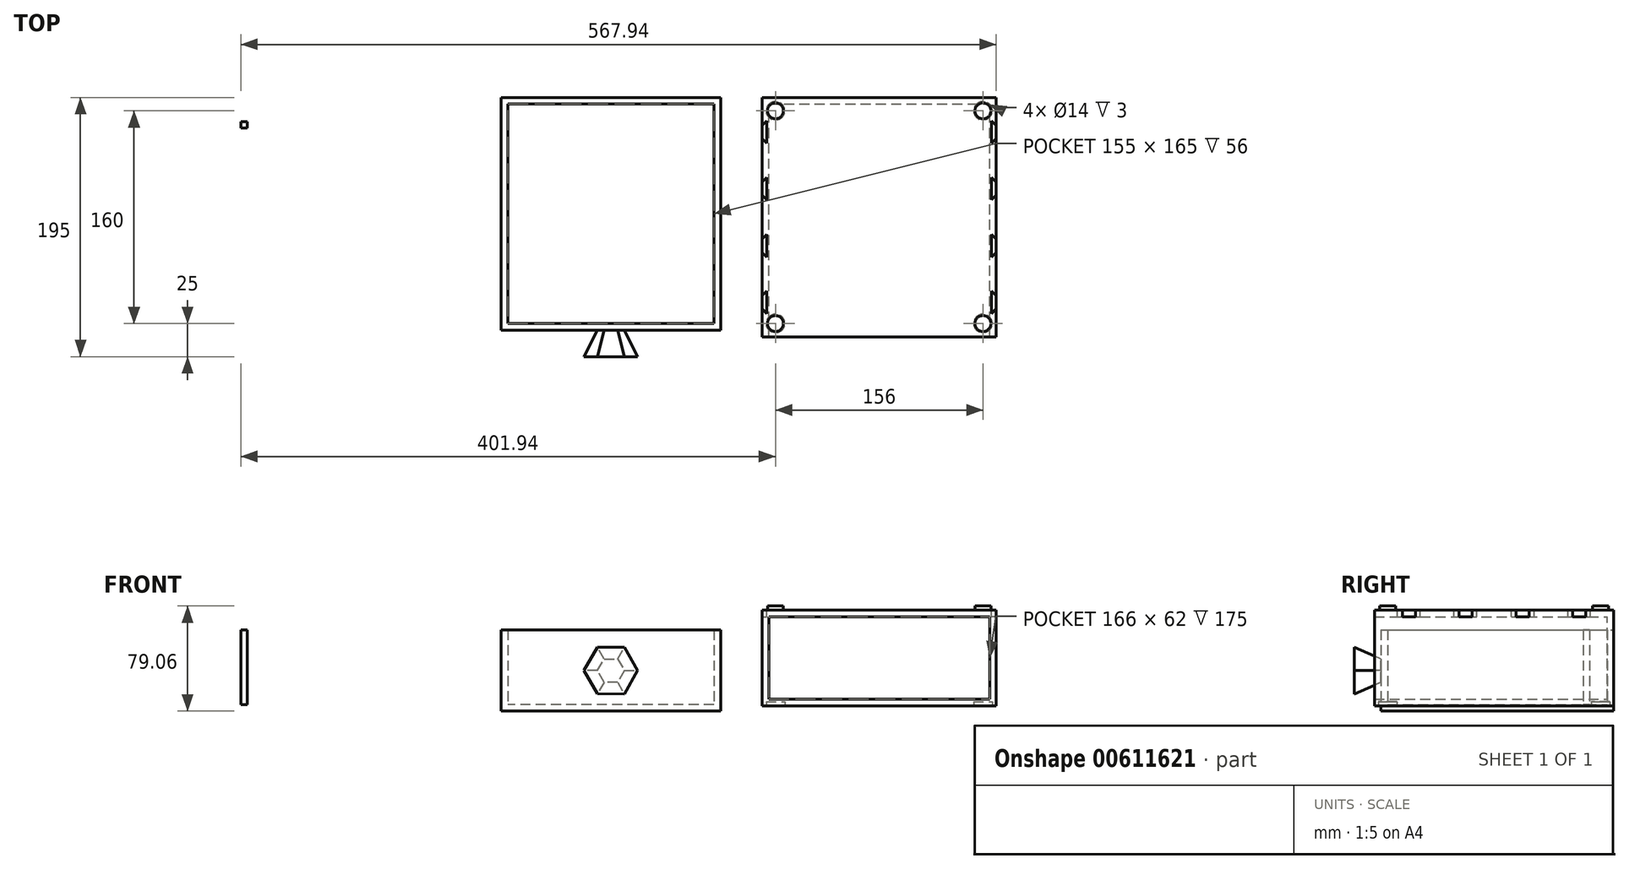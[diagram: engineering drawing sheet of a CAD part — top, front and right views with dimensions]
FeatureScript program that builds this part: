
annotation { "Feature Type Name" : "Feature", "Feature Type Description" : "" }
export const myFeature = defineFeature(function(context is Context, id is Id, definition is map)
    precondition{}
    {
        {
            var Q0;
            Q0=qCreatedBy(makeId("Front.planeOp"),FACE);
            var sketch = newSketch(context, id + "F0", { "sketchPlane" : qUnion([Q0])});
            skLineSegment(sketch, "E0.bottom", {"start": v(-21.74, -12.57) * mm, "end": v(144.26, -12.57) * mm});
            skLineSegment(sketch, "E0.top", {"start": v(-21.74, 49.43) * mm, "end": v(144.26, 49.43) * mm});
            skLineSegment(sketch, "E0.left", {"start": v(-21.74, -12.57) * mm, "end": v(-21.74, 49.43) * mm});
            skLineSegment(sketch, "E0.right", {"start": v(144.26, -12.57) * mm, "end": v(144.26, 49.43) * mm});
            skLineSegment(sketch, "E1.bottom", {"start": v(-26.74, -17.57) * mm, "end": v(149.26, -17.57) * mm});
            skLineSegment(sketch, "E1.top", {"start": v(-26.74, 54.43) * mm, "end": v(149.26, 54.43) * mm});
            skLineSegment(sketch, "E1.left", {"start": v(-26.74, -17.57) * mm, "end": v(-26.74, 54.43) * mm});
            skLineSegment(sketch, "E1.right", {"start": v(149.26, -17.57) * mm, "end": v(149.26, 54.43) * mm});
            skSolve(sketch);
        }
        {
            var Q0;
            Q0=makeQuery(id+"F0.imprint","IMPRINT",FACE,{"disambiguationData":[TD([[makeQuery(id+"F0.imprint","IMPRINT",EDGE,{"derivedFrom":sQuery(id+"F0.wireOp",EDGE,"E0.bottom")}),1.0]])]});
            extrude(context, id + "F1", {"entities" : qUnion([Q0]), "depth" : 5 * mm, "offsetDistance" : 25 * mm});
        }
        {
            var Q0;
            Q0=makeQuery(id+"F0.imprint","IMPRINT",FACE,{"disambiguationData":[TD([[makeQuery(id+"F0.imprint","IMPRINT",EDGE,{"derivedFrom":sQuery(id+"F0.wireOp",EDGE,"E0.bottom")}),-1.0]])]});
            extrude(context, id + "F2", {"entities" : qUnion([Q0]), "operationType" : NewBodyOperationType.ADD, "depth" : 180 * mm, "offsetDistance" : 25 * mm});
        }
        {
            var Q0;
            Q0=qCreatedBy(makeId("Front.planeOp"),FACE);
            var sketch = newSketch(context, id + "F3", { "sketchPlane" : qUnion([Q0])});
            skLineSegment(sketch, "E2.bottom", {"start": v(-57.99, 39.37) * mm, "end": v(-222.99, 39.37) * mm});
            skLineSegment(sketch, "E2.top", {"start": v(-57.99, -21.63) * mm, "end": v(-222.99, -21.63) * mm});
            skLineSegment(sketch, "E2.left", {"start": v(-57.99, 39.37) * mm, "end": v(-57.99, -21.63) * mm});
            skLineSegment(sketch, "E2.right", {"start": v(-222.99, 39.37) * mm, "end": v(-222.99, -21.63) * mm});
            skSolve(sketch);
        }
        {
            var Q0;
            Q0 = qSketchRegion(id + "F3", true);
            var Q1;
            Q1=makeQuery(id+"F3.imprint","IMPRINT",FACE,{"disambiguationData":[TD([[makeQuery(id+"F3.imprint","IMPRINT",EDGE,{"derivedFrom":sQuery(id+"F3.wireOp",EDGE,"E2.bottom")}),1.0]])]});
            extrude(context, id + "F4", {"entities" : qUnion([Q0, Q1]), "depth" : 175 * mm, "offsetDistance" : 25 * mm});
        }
        {
            var Q0;
            Q0=makeQuery(id+"F4.opExtrude","SWEPT_FACE",FACE,{"disambiguationData":[OSD([sQuery(id+"F3.wireOp",EDGE,"E2.bottom")])]});
            shell(context, id + "F5", {"entities" : qUnion([Q0]), "thickness" : 5 * mm});
        }
        {
            var Q0;
            Q0=makeQuery(id+"F4.opExtrude","CAP_FACE",FACE,{"disambiguationData":[OSD([sQuery(id+"F3.wireOp",EDGE,"E2.bottom"),sQuery(id+"F3.wireOp",EDGE,"E2.top"),sQuery(id+"F3.wireOp",EDGE,"E2.left"),sQuery(id+"F3.wireOp",EDGE,"E2.right")])],"isStart":false});
            var sketch = newSketch(context, id + "F6", { "sketchPlane" : qUnion([Q0])});
            skLineSegment(sketch, "E3", {"start": v(-222.99, 25.49) * mm, "end": v(-57.99, 25.49) * mm, "construction": true});
            skLineSegment(sketch, "E4", {"start": v(-146.55, 39.37) * mm, "end": v(-146.55, -21.63) * mm, "construction": true});
            skPoint(sketch, "E5", {"position": v(-146.55, 8.87) * mm});
            skPoint(sketch, "E6", {"position": v(-140.49, 25.49) * mm});
            skPoint(sketch, "E7.middle", {"position": v(-140.49, 8.87) * mm});
            skCircle(sketch, "E8.cCircle", {"center": v(-140.49, 8.87) * mm, "radius": 8.75 * mm, "construction": true});
            skLineSegment(sketch, "E8.0", {"start": v(-135.42, 17.61) * mm, "end": v(-130.38, 8.85) * mm});
            skLineSegment(sketch, "E8.1", {"start": v(-130.38, 8.85) * mm, "end": v(-135.46, 0.11) * mm});
            skLineSegment(sketch, "E8.2", {"start": v(-135.46, 0.11) * mm, "end": v(-145.56, 0.13) * mm});
            skLineSegment(sketch, "E8.3", {"start": v(-145.56, 0.13) * mm, "end": v(-150.6, 8.9) * mm});
            skLineSegment(sketch, "E8.4", {"start": v(-150.6, 8.9) * mm, "end": v(-145.52, 17.63) * mm});
            skLineSegment(sketch, "E8.5", {"start": v(-145.52, 17.63) * mm, "end": v(-135.42, 17.61) * mm});
            skPoint(sketch, "E8.0.midPoint", {"position": v(-132.9, 13.23) * mm});
            skSolve(sketch);
        }
        {
            var Q0;
            Q0=makeQuery(id+"F6.imprint","IMPRINT",FACE,{"disambiguationData":[TD([[makeQuery(id+"F6.imprint","IMPRINT",EDGE,{"derivedFrom":sQuery(id+"F6.wireOp",EDGE,"E8.0")}),1.0]])]});
            cPlane(context, id + "F7", {"entities" : qUnion([Q0]), "cplaneType" : CPlaneType.OFFSET, "offset" : 20 * mm, "width" : 150 * mm, "height" : 150 * mm});
        }
        {
            var Q0;
            Q0=qCreatedBy(id+"F7.planeOp",FACE);
            var sketch = newSketch(context, id + "F8", { "sketchPlane" : qUnion([Q0])});
            skCircle(sketch, "E9.cCircle", {"center": v(-140.49, 8.87) * mm, "radius": 17.5 * mm, "construction": true});
            skLineSegment(sketch, "E9.0", {"start": v(-130.34, 26.35) * mm, "end": v(-120.28, 8.83) * mm});
            skLineSegment(sketch, "E9.1", {"start": v(-120.28, 8.83) * mm, "end": v(-130.42, -8.65) * mm});
            skLineSegment(sketch, "E9.2", {"start": v(-130.42, -8.65) * mm, "end": v(-150.63, -8.6) * mm});
            skLineSegment(sketch, "E9.3", {"start": v(-150.63, -8.6) * mm, "end": v(-160.7, 8.92) * mm});
            skLineSegment(sketch, "E9.4", {"start": v(-160.7, 8.92) * mm, "end": v(-150.55, 26.4) * mm});
            skLineSegment(sketch, "E9.5", {"start": v(-150.55, 26.4) * mm, "end": v(-130.34, 26.35) * mm});
            skPoint(sketch, "E9.0.midPoint", {"position": v(-125.31, 17.59) * mm});
            skSolve(sketch);
        }
        {
            var Q1;
            Q1=makeQuery(id+"F6.imprint","IMPRINT",FACE,{"disambiguationData":[TD([[makeQuery(id+"F6.imprint","IMPRINT",EDGE,{"derivedFrom":sQuery(id+"F6.wireOp",EDGE,"E8.0")}),-1.0]])]});
            var Q2;
            Q2=makeQuery(id+"F8.imprint","IMPRINT",FACE,{"disambiguationData":[TD([[makeQuery(id+"F8.imprint","IMPRINT",EDGE,{"derivedFrom":sQuery(id+"F8.wireOp",EDGE,"E9.0")}),-1.0]])]});
            loft(context, id + "F9", {"operationType" : NewBodyOperationType.ADD, "sheetProfilesArray" : [{ "sheetProfileEntities" : qUnion([Q1]) }, { "sheetProfileEntities" : qUnion([Q2]) }]});
        }
        {
            var Q0;
            Q0=makeQuery(id+"F2.opExtrude","SWEPT_FACE",FACE,{"disambiguationData":[OSD([sQuery(id+"F0.wireOp",EDGE,"E1.bottom")])]});
            var sketch = newSketch(context, id + "F10", { "sketchPlane" : qUnion([Q0])});
            skLineSegment(sketch, "E10", {"start": v(-26.74, 170) * mm, "end": v(149.26, 170) * mm, "construction": true});
            skLineSegment(sketch, "E11", {"start": v(-16.74, 180) * mm, "end": v(-16.74, 0) * mm, "construction": true});
            skLineSegment(sketch, "E12", {"start": v(139.26, 180) * mm, "end": v(139.26, 0) * mm, "construction": true});
            skLineSegment(sketch, "E13", {"start": v(-26.74, 10) * mm, "end": v(149.26, 10) * mm, "construction": true});
            skCircle(sketch, "E14", {"center": v(-16.74, 170) * mm, "radius": 6 * mm});
            skCircle(sketch, "E15", {"center": v(139.26, 170) * mm, "radius": 6 * mm});
            skCircle(sketch, "E16", {"center": v(139.26, 10) * mm, "radius": 6 * mm});
            skCircle(sketch, "E17", {"center": v(-16.74, 10) * mm, "radius": 6 * mm});
            skCircle(sketch, "E18", {"center": v(-16.74, 170) * mm, "radius": 7 * mm});
            skCircle(sketch, "E19", {"center": v(139.26, 170) * mm, "radius": 7 * mm});
            skCircle(sketch, "E20", {"center": v(139.26, 10) * mm, "radius": 7 * mm});
            skCircle(sketch, "E21", {"center": v(-16.74, 10) * mm, "radius": 7 * mm});
            skSolve(sketch);
        }
        {
            var Q0;
            Q0=makeQuery(id+"F10.imprint","IMPRINT",FACE,{"disambiguationData":[TD([[makeQuery(id+"F10.imprint","IMPRINT",EDGE,{"derivedFrom":sQuery(id+"F10.wireOp",EDGE,"E14")}),1.0]])]});
            var Q1;
            Q1=makeQuery(id+"F10.imprint","IMPRINT",FACE,{"disambiguationData":[TD([[makeQuery(id+"F10.imprint","IMPRINT",EDGE,{"derivedFrom":sQuery(id+"F10.wireOp",EDGE,"E15")}),1.0]])]});
            var Q2;
            Q2=makeQuery(id+"F10.imprint","IMPRINT",FACE,{"disambiguationData":[TD([[makeQuery(id+"F10.imprint","IMPRINT",EDGE,{"derivedFrom":sQuery(id+"F10.wireOp",EDGE,"E16")}),1.0]])]});
            var Q3;
            Q3=makeQuery(id+"F10.imprint","IMPRINT",FACE,{"disambiguationData":[TD([[makeQuery(id+"F10.imprint","IMPRINT",EDGE,{"derivedFrom":sQuery(id+"F10.wireOp",EDGE,"E17")}),1.0]])]});
            extrude(context, id + "F11", {"entities" : qUnion([Q0, Q1, Q2, Q3]), "operationType" : NewBodyOperationType.ADD, "oppositeDirection" : true, "depth" : 75 * mm, "offsetDistance" : 25 * mm});
        }
        {
            var Q0;
            Q0 = qSketchRegion(id + "F10", true);
            extrude(context, id + "F12", {"entities" : qUnion([Q0]), "operationType" : NewBodyOperationType.REMOVE, "oppositeDirection" : true, "depth" : 3 * mm, "offsetDistance" : 25 * mm});
        }
        {
            var Q0;
            Q0=makeQuery(id+"F0.imprint","IMPRINT",FACE,{"disambiguationData":[TD([[makeQuery(id+"F0.imprint","IMPRINT",EDGE,{"derivedFrom":sQuery(id+"F0.wireOp",EDGE,"E0.bottom")}),1.0]])]});
            extrude(context, id + "F13", {"entities" : qUnion([Q0]), "operationType" : NewBodyOperationType.REMOVE, "depth" : 314 * mm, "offsetDistance" : 25 * mm});
        }
        {
            var Q0;
            Q0=makeQuery(id+"F0.imprint","IMPRINT",FACE,{"disambiguationData":[TD([[makeQuery(id+"F0.imprint","IMPRINT",EDGE,{"derivedFrom":sQuery(id+"F0.wireOp",EDGE,"E0.bottom")}),1.0]])]});
            extrude(context, id + "F14", {"entities" : qUnion([Q0]), "operationType" : NewBodyOperationType.ADD, "depth" : 5 * mm, "offsetDistance" : 25 * mm});
        }
        {
            var Q0;
            Q0=makeQuery(id+"F5.opShell","OFFSET_FACE",FACE,{"disambiguationData":[OSD([sQuery(id+"F3.wireOp",EDGE,"E2.top")])]});
            var sketch = newSketch(context, id + "F15", { "sketchPlane" : qUnion([Q0])});
            skLineSegment(sketch, "E22", {"start": v(-208.24, -5) * mm, "end": v(-208.24, -170) * mm, "construction": true});
            skLineSegment(sketch, "E23", {"start": v(-217.99, -154) * mm, "end": v(-62.99, -154) * mm, "construction": true});
            skLineSegment(sketch, "E24.bottom", {"start": v(-493.68, 61.88) * mm, "end": v(-338.68, 61.88) * mm});
            skLineSegment(sketch, "E24.top", {"start": v(-493.68, -103.12) * mm, "end": v(-338.68, -103.12) * mm});
            skLineSegment(sketch, "E24.left", {"start": v(-493.68, 61.88) * mm, "end": v(-493.68, -103.12) * mm});
            skLineSegment(sketch, "E24.right", {"start": v(-338.68, 61.88) * mm, "end": v(-338.68, -103.12) * mm});
            skLineSegment(sketch, "E25.bottom", {"start": v(-418.68, 61.88) * mm, "end": v(-413.68, 61.88) * mm});
            skLineSegment(sketch, "E25.top", {"start": v(-418.68, -103.12) * mm, "end": v(-413.68, -103.12) * mm});
            skLineSegment(sketch, "E25.left", {"start": v(-418.68, 61.88) * mm, "end": v(-418.68, -103.12) * mm});
            skLineSegment(sketch, "E25.right", {"start": v(-413.68, 61.88) * mm, "end": v(-413.68, -103.12) * mm});
            skPoint(sketch, "E26", {"position": v(-416.18, 61.88) * mm});
            skPoint(sketch, "E27", {"position": v(-493.68, -20.62) * mm});
            skLineSegment(sketch, "E28.bottom", {"start": v(-493.68, -18.12) * mm, "end": v(-338.68, -18.12) * mm});
            skLineSegment(sketch, "E28.top", {"start": v(-493.68, -23.12) * mm, "end": v(-338.68, -23.12) * mm});
            skLineSegment(sketch, "E28.left", {"start": v(-493.68, -18.12) * mm, "end": v(-493.68, -23.12) * mm});
            skLineSegment(sketch, "E28.right", {"start": v(-338.68, -18.12) * mm, "end": v(-338.68, -23.12) * mm});
            skSolve(sketch);
        }
        {
            var Q0;
            {var subQ0=sQuery(id+"F15.wireOp",EDGE,"E25.bottom");Q0=makeQuery(id+"F15.imprint","IMPRINT",FACE,{"disambiguationData":[TD([[makeQuery(id+"F15.imprint","IMPRINT",EDGE,{"derivedFrom":subQ0}),-1.0]])]});}
            var Q1;
            {var subQ5=sQuery(id+"F15.wireOp",EDGE,"E28.left");Q1=makeQuery(id+"F15.imprint","IMPRINT",FACE,{"disambiguationData":[TD([[makeQuery(id+"F15.imprint","IMPRINT",EDGE,{"derivedFrom":subQ5}),1.0]])]});}
            var Q2;
            {var subQ0=sQuery(id+"F15.wireOp",EDGE,"E28.bottom");var subQ1=sQuery(id+"F15.wireOp",EDGE,"E25.left");var subQ2=makeQuery(id+"F15.imprint","INTERSECT",VERTEX,{"derivedFrom":[subQ1,subQ0]});Q2=makeQuery(id+"F15.imprint","IMPRINT",FACE,{"disambiguationData":[TD([[makeQuery(id+"F15.imprint","IMPRINT",EDGE,{"disambiguationData":[TD([[subQ2,-1.0]])],"derivedFrom":subQ1}),1.0]])]});}
            var Q3;
            {var subQ5=sQuery(id+"F15.wireOp",EDGE,"E28.right");Q3=makeQuery(id+"F15.imprint","IMPRINT",FACE,{"disambiguationData":[TD([[makeQuery(id+"F15.imprint","IMPRINT",EDGE,{"derivedFrom":subQ5}),-1.0]])]});}
            var Q4;
            {var subQ0=sQuery(id+"F15.wireOp",EDGE,"E25.top");Q4=makeQuery(id+"F15.imprint","IMPRINT",FACE,{"disambiguationData":[TD([[makeQuery(id+"F15.imprint","IMPRINT",EDGE,{"derivedFrom":subQ0}),1.0]])]});}
            extrude(context, id + "F16", {"entities" : qUnion([Q0, Q1, Q2, Q3, Q4]), "depth" : 56 * mm, "offsetDistance" : 25 * mm});
        }
        {
            var Q0;
            Q0=makeQuery(id+"F2.opExtrude","SWEPT_FACE",FACE,{"disambiguationData":[OSD([sQuery(id+"F0.wireOp",EDGE,"E1.top")])]});
            var sketch = newSketch(context, id + "F17", { "sketchPlane" : qUnion([Q0])});
            skLineSegment(sketch, "E29", {"start": v(149.26, -149) * mm, "end": v(145.72, -145.46) * mm});
            skLineSegment(sketch, "E30", {"start": v(145.72, -162.54) * mm, "end": v(145.72, -145.46) * mm});
            skLineSegment(sketch, "E31", {"start": v(145.72, -162.54) * mm, "end": v(149.26, -159) * mm});
            skLineSegment(sketch, "E32", {"start": v(149.26, -149) * mm, "end": v(149.26, -159) * mm});
            skPoint(sketch, "E33", {"position": v(139.26, -16) * mm});
            skPoint(sketch, "E34", {"position": v(139.26, -164) * mm});
            skLineSegment(sketch, "E35", {"start": v(139.26, -164) * mm, "end": v(149.26, -164) * mm, "construction": true});
            skLineSegment(sketch, "E36", {"start": v(149.26, -164) * mm, "end": v(149.26, -154) * mm, "construction": true});
            skLineSegment(sketch, "E37", {"start": v(139.26, -16) * mm, "end": v(149.26, -16) * mm, "construction": true});
            skLineSegment(sketch, "E38", {"start": v(149.26, -16) * mm, "end": v(149.26, -26) * mm, "construction": true});
            skPoint(sketch, "E39", {"position": v(149.26, -154) * mm});
            skLineSegment(sketch, "E40", {"start": v(149.26, -21) * mm, "end": v(145.72, -17.46) * mm});
            skLineSegment(sketch, "E41", {"start": v(145.72, -34.54) * mm, "end": v(145.72, -17.46) * mm});
            skLineSegment(sketch, "E42", {"start": v(145.72, -34.54) * mm, "end": v(149.26, -31) * mm});
            skLineSegment(sketch, "E43", {"start": v(149.26, -21) * mm, "end": v(149.26, -31) * mm});
            skPoint(sketch, "E44", {"position": v(149.26, -26) * mm});
            skPoint(sketch, "E45", {"position": v(149.26, -111.5) * mm});
            skPoint(sketch, "E46", {"position": v(149.26, -68.5) * mm});
            skLineSegment(sketch, "E47", {"start": v(149.26, -106.5) * mm, "end": v(145.72, -102.96) * mm});
            skLineSegment(sketch, "E48", {"start": v(145.72, -120.04) * mm, "end": v(145.72, -102.96) * mm});
            skLineSegment(sketch, "E49", {"start": v(145.72, -120.04) * mm, "end": v(149.26, -116.5) * mm});
            skLineSegment(sketch, "E50", {"start": v(149.26, -106.5) * mm, "end": v(149.26, -116.5) * mm});
            skLineSegment(sketch, "E51", {"start": v(149.26, -63.5) * mm, "end": v(145.72, -59.96) * mm});
            skLineSegment(sketch, "E52", {"start": v(145.72, -77.04) * mm, "end": v(145.72, -59.96) * mm});
            skLineSegment(sketch, "E53", {"start": v(145.72, -77.04) * mm, "end": v(149.26, -73.5) * mm});
            skLineSegment(sketch, "E54", {"start": v(149.26, -63.5) * mm, "end": v(149.26, -73.5) * mm});
            skLineSegment(sketch, "E55.MirrorCS", {"start": v(-23.2, -120.04) * mm, "end": v(-26.74, -116.5) * mm});
            skLineSegment(sketch, "E56.MirrorCS", {"start": v(-26.74, -21) * mm, "end": v(-23.2, -17.46) * mm});
            skLineSegment(sketch, "E57.MirrorCS", {"start": v(-23.2, -77.04) * mm, "end": v(-26.74, -73.5) * mm});
            skLineSegment(sketch, "E58.MirrorCS", {"start": v(-26.74, -149) * mm, "end": v(-23.2, -145.46) * mm});
            skLineSegment(sketch, "E59.MirrorCS", {"start": v(-23.2, -162.54) * mm, "end": v(-26.74, -159) * mm});
            skLineSegment(sketch, "E60.MirrorCS", {"start": v(-23.2, -34.54) * mm, "end": v(-26.74, -31) * mm});
            skLineSegment(sketch, "E61.MirrorCS", {"start": v(-26.74, -63.5) * mm, "end": v(-23.2, -59.96) * mm});
            skLineSegment(sketch, "E62.MirrorCS", {"start": v(-26.74, -106.5) * mm, "end": v(-23.2, -102.96) * mm});
            skLineSegment(sketch, "E63.MirrorCS", {"start": v(-23.2, -162.54) * mm, "end": v(-23.2, -145.46) * mm});
            skLineSegment(sketch, "E64.MirrorCS", {"start": v(-23.2, -77.04) * mm, "end": v(-23.2, -59.96) * mm});
            skLineSegment(sketch, "E65.MirrorCS", {"start": v(-26.74, -106.5) * mm, "end": v(-26.74, -116.5) * mm});
            skLineSegment(sketch, "E66.MirrorCS", {"start": v(-23.2, -120.04) * mm, "end": v(-23.2, -102.96) * mm});
            skLineSegment(sketch, "E67.MirrorCS", {"start": v(-23.2, -34.54) * mm, "end": v(-23.2, -17.46) * mm});
            skLineSegment(sketch, "E68.MirrorCS", {"start": v(-26.74, -63.5) * mm, "end": v(-26.74, -73.5) * mm});
            skLineSegment(sketch, "E69.MirrorCS", {"start": v(-26.74, -149) * mm, "end": v(-26.74, -159) * mm});
            skLineSegment(sketch, "E70.MirrorCS", {"start": v(-26.74, -21) * mm, "end": v(-26.74, -31) * mm});
            skPoint(sketch, "E71", {"position": v(-26.74, -26) * mm});
            skPoint(sketch, "E72", {"position": v(-26.74, -68.5) * mm});
            skPoint(sketch, "E73", {"position": v(-26.74, -111.5) * mm});
            skPoint(sketch, "E74", {"position": v(-26.74, -154) * mm});
            skLineSegment(sketch, "E75", {"start": v(149.26, -26) * mm, "end": v(-26.74, -26) * mm, "construction": true});
            skLineSegment(sketch, "E76", {"start": v(149.26, -68.5) * mm, "end": v(-26.74, -68.5) * mm, "construction": true});
            skLineSegment(sketch, "E77", {"start": v(149.26, -111.5) * mm, "end": v(-26.74, -111.5) * mm, "construction": true});
            skLineSegment(sketch, "E78", {"start": v(149.26, -154) * mm, "end": v(-26.74, -154) * mm, "construction": true});
            skSolve(sketch);
        }
        {
            var Q0;
            Q0=makeQuery(id+"F17.imprint","IMPRINT",FACE,{"disambiguationData":[TD([[makeQuery(id+"F17.imprint","IMPRINT",EDGE,{"derivedFrom":sQuery(id+"F17.wireOp",EDGE,"E56.MirrorCS")}),-1.0]])]});
            var Q1;
            Q1=makeQuery(id+"F17.imprint","IMPRINT",FACE,{"disambiguationData":[TD([[makeQuery(id+"F17.imprint","IMPRINT",EDGE,{"derivedFrom":sQuery(id+"F17.wireOp",EDGE,"E57.MirrorCS")}),-1.0]])]});
            var Q2;
            Q2=makeQuery(id+"F17.imprint","IMPRINT",FACE,{"disambiguationData":[TD([[makeQuery(id+"F17.imprint","IMPRINT",EDGE,{"derivedFrom":sQuery(id+"F17.wireOp",EDGE,"E55.MirrorCS")}),-1.0]])]});
            var Q3;
            Q3=makeQuery(id+"F17.imprint","IMPRINT",FACE,{"disambiguationData":[TD([[makeQuery(id+"F17.imprint","IMPRINT",EDGE,{"derivedFrom":sQuery(id+"F17.wireOp",EDGE,"E58.MirrorCS")}),-1.0]])]});
            var Q4;
            Q4=makeQuery(id+"F17.imprint","IMPRINT",FACE,{"disambiguationData":[TD([[makeQuery(id+"F17.imprint","IMPRINT",EDGE,{"derivedFrom":sQuery(id+"F17.wireOp",EDGE,"E29")}),1.0]])]});
            var Q5;
            Q5=makeQuery(id+"F17.imprint","IMPRINT",FACE,{"disambiguationData":[TD([[makeQuery(id+"F17.imprint","IMPRINT",EDGE,{"derivedFrom":sQuery(id+"F17.wireOp",EDGE,"E47")}),1.0]])]});
            var Q6;
            Q6=makeQuery(id+"F17.imprint","IMPRINT",FACE,{"disambiguationData":[TD([[makeQuery(id+"F17.imprint","IMPRINT",EDGE,{"derivedFrom":sQuery(id+"F17.wireOp",EDGE,"E51")}),1.0]])]});
            var Q7;
            Q7=makeQuery(id+"F17.imprint","IMPRINT",FACE,{"disambiguationData":[TD([[makeQuery(id+"F17.imprint","IMPRINT",EDGE,{"derivedFrom":sQuery(id+"F17.wireOp",EDGE,"E40")}),1.0]])]});
            extrude(context, id + "F18", {"entities" : qUnion([Q0, Q1, Q2, Q3, Q4, Q5, Q6, Q7]), "operationType" : NewBodyOperationType.REMOVE, "oppositeDirection" : true, "depth" : 5 * mm, "offsetDistance" : 25 * mm});
        }
        {
            var Q0;
            Q0=makeQuery(id+"F10.imprint","IMPRINT",FACE,{"disambiguationData":[TD([[makeQuery(id+"F10.imprint","IMPRINT",EDGE,{"derivedFrom":sQuery(id+"F10.wireOp",EDGE,"E17")}),1.0]])]});
            var Q1;
            Q1=makeQuery(id+"F10.imprint","IMPRINT",FACE,{"disambiguationData":[TD([[makeQuery(id+"F10.imprint","IMPRINT",EDGE,{"derivedFrom":sQuery(id+"F10.wireOp",EDGE,"E16")}),1.0]])]});
            var Q2;
            Q2=makeQuery(id+"F10.imprint","IMPRINT",FACE,{"disambiguationData":[TD([[makeQuery(id+"F10.imprint","IMPRINT",EDGE,{"derivedFrom":sQuery(id+"F10.wireOp",EDGE,"E15")}),1.0]])]});
            var Q3;
            Q3=makeQuery(id+"F10.imprint","IMPRINT",FACE,{"disambiguationData":[TD([[makeQuery(id+"F10.imprint","IMPRINT",EDGE,{"derivedFrom":sQuery(id+"F10.wireOp",EDGE,"E14")}),1.0]])]});
            extrude(context, id + "F19", {"entities" : qUnion([Q0, Q1, Q2, Q3]), "operationType" : NewBodyOperationType.REMOVE, "oppositeDirection" : true, "depth" : 3 * mm, "offsetDistance" : 25 * mm, "hasDraft" : true, "draftAngle" : 3 * degree});
        }
    });
